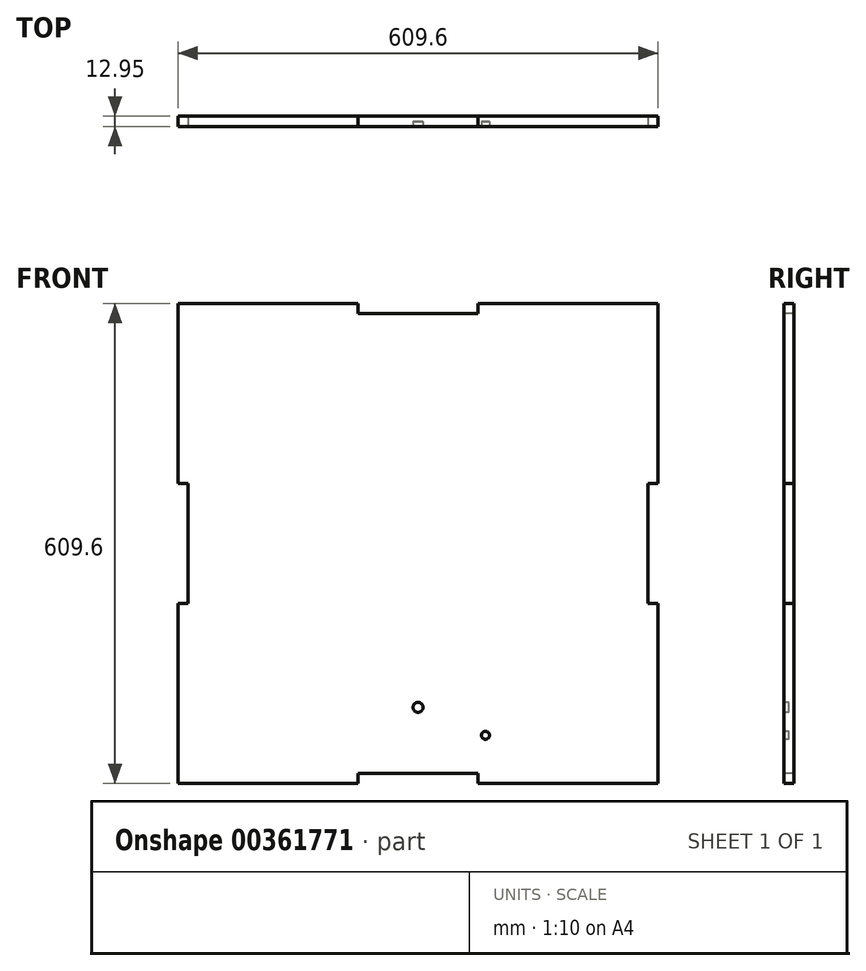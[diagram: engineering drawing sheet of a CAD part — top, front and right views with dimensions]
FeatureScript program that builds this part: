
annotation { "Feature Type Name" : "Feature", "Feature Type Description" : "" }
export const myFeature = defineFeature(function(context is Context, id is Id, definition is map)
    precondition{}
    {
        {
            var Q0;
            Q0=qCreatedBy(makeId("Front.planeOp"),FACE);
            var sketch = newSketch(context, id + "F0", { "sketchPlane" : qUnion([Q0])});
            skLineSegment(sketch, "E0.bottom", {"start": v(-304.8, 304.8) * mm, "end": v(304.8, 304.8) * mm});
            skLineSegment(sketch, "E0.top", {"start": v(-304.8, -304.8) * mm, "end": v(304.8, -304.8) * mm});
            skLineSegment(sketch, "E0.left", {"start": v(-304.8, 304.8) * mm, "end": v(-304.8, -304.8) * mm});
            skLineSegment(sketch, "E0.right", {"start": v(304.8, 304.8) * mm, "end": v(304.8, -304.8) * mm});
            skPoint(sketch, "E0.middle", {"position": v(0, 0) * mm});
            skSolve(sketch);
        }
        {
            var Q0;
            Q0=makeQuery(id+"F0.imprint","IMPRINT",FACE,{"disambiguationData":[TD([[makeQuery(id+"F0.imprint","IMPRINT",EDGE,{"derivedFrom":sQuery(id+"F0.wireOp",EDGE,"E0.bottom")}),-1.0]])]});
            extrude(context, id + "F1", {"entities" : qUnion([Q0]), "depth" : 12.95 * mm});
        }
        {
            var Q0;
            Q0=makeQuery(id+"F1.opExtrude","CAP_FACE",FACE,{"disambiguationData":[OSD([sQuery(id+"F0.wireOp",EDGE,"E0.bottom"),sQuery(id+"F0.wireOp",EDGE,"E0.top"),sQuery(id+"F0.wireOp",EDGE,"E0.left"),sQuery(id+"F0.wireOp",EDGE,"E0.right")])],"isStart":false});
            var sketch = newSketch(context, id + "F2", { "sketchPlane" : qUnion([Q0])});
            skCircle(sketch, "E1", {"center": v(85.62, -243.75) * mm, "radius": 5.08 * mm});
            skLineSegment(sketch, "E2", {"start": v(76.2, -304.8) * mm, "end": v(76.2, -292.1) * mm});
            skLineSegment(sketch, "E3", {"start": v(76.2, -292.1) * mm, "end": v(-76.2, -292.1) * mm});
            skLineSegment(sketch, "E4", {"start": v(-76.2, -292.1) * mm, "end": v(-76.2, -304.8) * mm});
            skLineSegment(sketch, "E5", {"start": v(304.8, -76.2) * mm, "end": v(292.1, -76.2) * mm});
            skLineSegment(sketch, "E6", {"start": v(292.1, -76.2) * mm, "end": v(292.1, 76.2) * mm});
            skLineSegment(sketch, "E7", {"start": v(292.1, 76.2) * mm, "end": v(304.8, 76.2) * mm});
            skLineSegment(sketch, "E8", {"start": v(76.2, 304.8) * mm, "end": v(76.2, 292.1) * mm});
            skLineSegment(sketch, "E9", {"start": v(76.2, 292.1) * mm, "end": v(-76.2, 292.1) * mm});
            skLineSegment(sketch, "E10", {"start": v(-76.2, 292.1) * mm, "end": v(-76.2, 304.8) * mm});
            skLineSegment(sketch, "E11", {"start": v(-304.8, 76.2) * mm, "end": v(-292.1, 76.2) * mm});
            skLineSegment(sketch, "E12", {"start": v(-292.1, 76.2) * mm, "end": v(-292.1, -76.2) * mm});
            skLineSegment(sketch, "E13", {"start": v(-292.1, -76.2) * mm, "end": v(-304.8, -76.2) * mm});
            skCircle(sketch, "E14", {"center": v(0, -208.2) * mm, "radius": 6.35 * mm});
            skSolve(sketch);
        }
        {
            var Q0;
            Q0=makeQuery(id+"F2.imprint","IMPRINT",FACE,{"disambiguationData":[TD([[makeQuery(id+"F2.imprint","IMPRINT",EDGE,{"derivedFrom":sQuery(id+"F2.wireOp",EDGE,"E14")}),1.0]])]});
            var Q1;
            Q1=makeQuery(id+"F2.imprint","IMPRINT",FACE,{"disambiguationData":[TD([[makeQuery(id+"F2.imprint","IMPRINT",EDGE,{"derivedFrom":sQuery(id+"F2.wireOp",EDGE,"E1")}),1.0]])]});
            extrude(context, id + "F3", {"entities" : qUnion([Q0, Q1]), "oppositeDirection" : true, "depth" : 6.35 * mm});
        }
        {
            var Q0;
            {var subQ0=sQuery(id+"F2.wireOp",EDGE,"E2");Q0=makeQuery(id+"F2.imprint","IMPRINT",FACE,{"disambiguationData":[TD([[makeQuery(id+"F2.imprint","IMPRINT",EDGE,{"derivedFrom":subQ0}),1.0]])]});}
            var Q1;
            {var subQ0=sQuery(id+"F2.wireOp",EDGE,"E5");Q1=makeQuery(id+"F2.imprint","IMPRINT",FACE,{"disambiguationData":[TD([[makeQuery(id+"F2.imprint","IMPRINT",EDGE,{"derivedFrom":subQ0}),-1.0]])]});}
            var Q2;
            {var subQ0=sQuery(id+"F2.wireOp",EDGE,"E8");Q2=makeQuery(id+"F2.imprint","IMPRINT",FACE,{"disambiguationData":[TD([[makeQuery(id+"F2.imprint","IMPRINT",EDGE,{"derivedFrom":subQ0}),-1.0]])]});}
            var Q3;
            {var subQ0=sQuery(id+"F2.wireOp",EDGE,"E11");Q3=makeQuery(id+"F2.imprint","IMPRINT",FACE,{"disambiguationData":[TD([[makeQuery(id+"F2.imprint","IMPRINT",EDGE,{"derivedFrom":subQ0}),-1.0]])]});}
            extrude(context, id + "F4", {"entities" : qUnion([Q0, Q1, Q2, Q3]), "operationType" : NewBodyOperationType.REMOVE, "oppositeDirection" : true, "depth" : 12.95 * mm});
        }
    });
